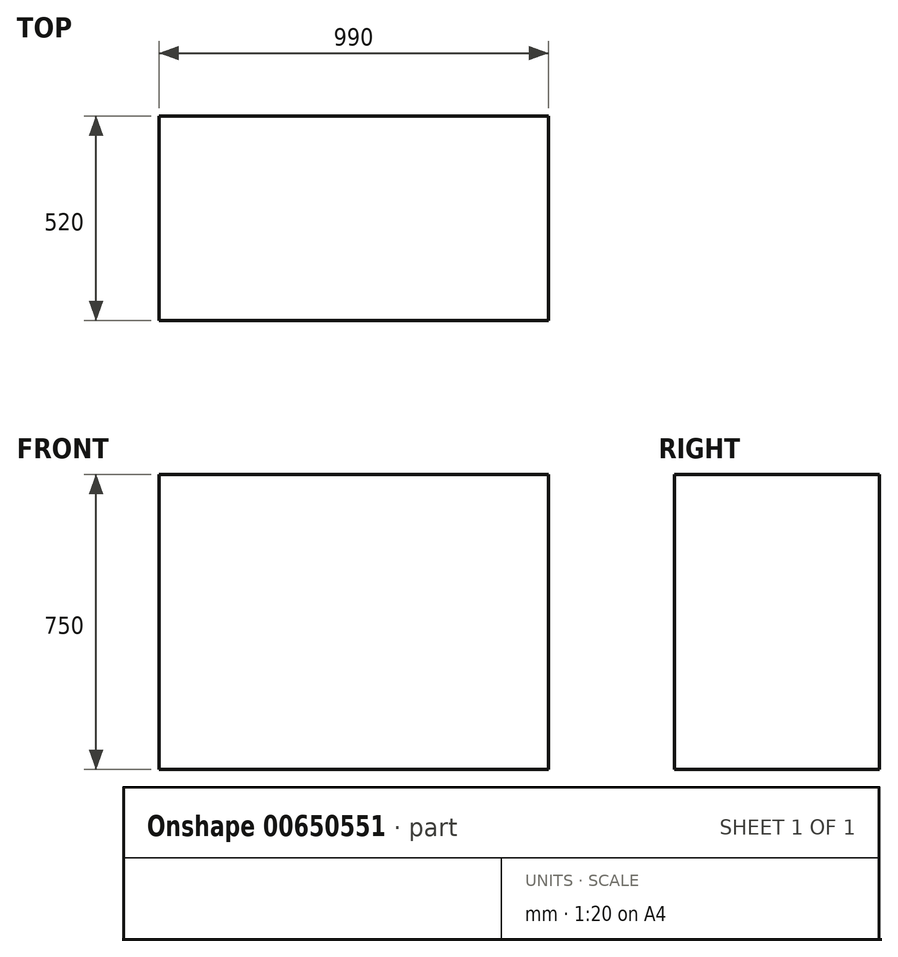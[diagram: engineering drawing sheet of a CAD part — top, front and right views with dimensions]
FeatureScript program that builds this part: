
annotation { "Feature Type Name" : "Feature", "Feature Type Description" : "" }
export const myFeature = defineFeature(function(context is Context, id is Id, definition is map)
    precondition{}
    {
        {
            var Q0;
            Q0=qCreatedBy(makeId("Top.planeOp"),FACE);
            var sketch = newSketch(context, id + "F0", { "sketchPlane" : qUnion([Q0])});
            skLineSegment(sketch, "E0.bottom", {"start": v(0, 0) * mm, "end": v(-990, 0) * mm});
            skLineSegment(sketch, "E0.top", {"start": v(0, 520) * mm, "end": v(-990, 520) * mm});
            skLineSegment(sketch, "E0.left", {"start": v(0, 0) * mm, "end": v(0, 520) * mm});
            skLineSegment(sketch, "E0.right", {"start": v(-990, 0) * mm, "end": v(-990, 520) * mm});
            skSolve(sketch);
        }
        {
            var Q0;
            Q0 = qSketchRegion(id + "F0", true);
            extrude(context, id + "F1", {"entities" : qUnion([Q0]), "depth" : 750 * mm, "offsetDistance" : 25 * mm});
        }
    });
